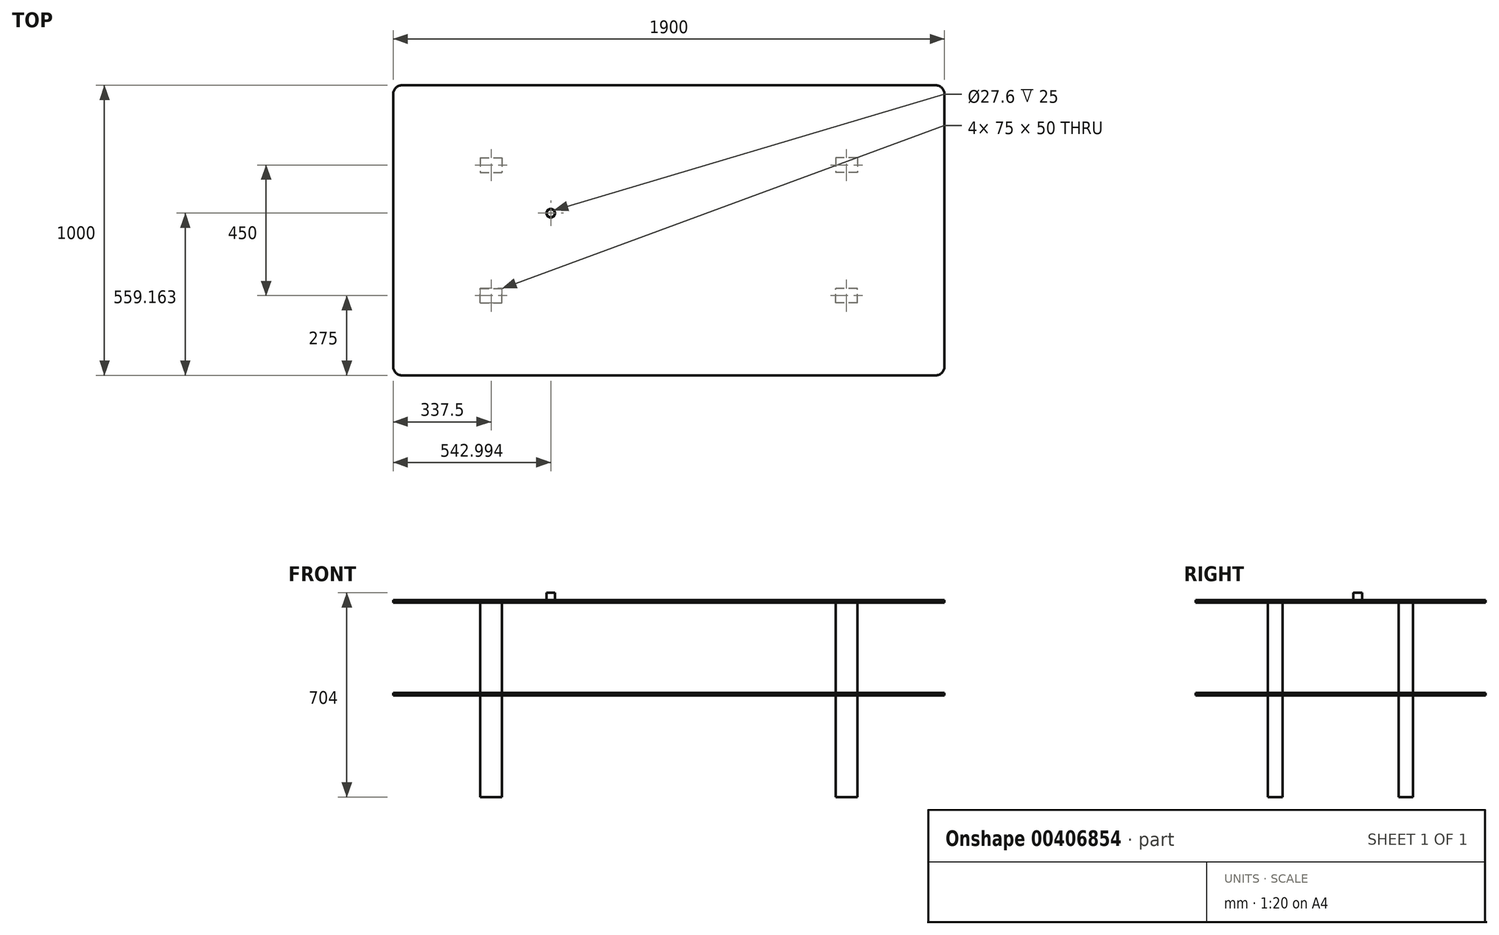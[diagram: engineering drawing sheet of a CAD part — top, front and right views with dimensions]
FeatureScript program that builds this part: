
annotation { "Feature Type Name" : "Feature", "Feature Type Description" : "" }
export const myFeature = defineFeature(function(context is Context, id is Id, definition is map)
    precondition{}
    {
        {
            var Q0;
            Q0=qCreatedBy(makeId("Top.planeOp"),FACE);
            var sketch = newSketch(context, id + "F0", { "sketchPlane" : qUnion([Q0])});
            skLineSegment(sketch, "E0.bottom", {"start": v(-920, 500) * mm, "end": v(920, 500) * mm});
            skLineSegment(sketch, "E0.top", {"start": v(-920, -500) * mm, "end": v(920, -500) * mm});
            skLineSegment(sketch, "E0.left", {"start": v(-950, 470) * mm, "end": v(-950, -470) * mm});
            skLineSegment(sketch, "E0.right", {"start": v(950, 470) * mm, "end": v(950, -470) * mm});
            skPoint(sketch, "E0.middle", {"position": v(0, 0) * mm});
            skPoint(sketch, "E1.visualSharp", {"position": v(-950, 500) * mm});
            skArc(sketch, "E1.filletArc", {"start": v(-920, 500) * mm, "mid": v(-941.21, 491.21) * mm, "end": v(-950, 470) * mm});
            skPoint(sketch, "E2.visualSharp", {"position": v(-950, -500) * mm});
            skArc(sketch, "E2.filletArc", {"start": v(-950, -470) * mm, "mid": v(-941.21, -491.21) * mm, "end": v(-920, -500) * mm});
            skPoint(sketch, "E3.visualSharp", {"position": v(950, -500) * mm});
            skArc(sketch, "E3.filletArc", {"start": v(920, -500) * mm, "mid": v(941.21, -491.21) * mm, "end": v(950, -470) * mm});
            skPoint(sketch, "E4.visualSharp", {"position": v(950, 500) * mm});
            skArc(sketch, "E4.filletArc", {"start": v(950, 470) * mm, "mid": v(941.21, 491.21) * mm, "end": v(920, 500) * mm});
            skLineSegment(sketch, "E5.bottom", {"start": v(-650, 200) * mm, "end": v(-575, 200) * mm});
            skLineSegment(sketch, "E5.top", {"start": v(-650, 250) * mm, "end": v(-575, 250) * mm});
            skLineSegment(sketch, "E5.left", {"start": v(-650, 250) * mm, "end": v(-650, 200) * mm});
            skLineSegment(sketch, "E5.right", {"start": v(-575, 250) * mm, "end": v(-575, 200) * mm});
            skLineSegment(sketch, "E6", {"start": v(0, 0) * mm, "end": v(0, 737.26) * mm, "construction": true});
            skPoint(sketch, "E6.endSnap0", {"position": v(0, 500) * mm});
            skLineSegment(sketch, "E7", {"start": v(0, 0) * mm, "end": v(1153.5, 0) * mm, "construction": true});
            skLineSegment(sketch, "E8.MirrorCS", {"start": v(575, 250) * mm, "end": v(575, 200) * mm});
            skLineSegment(sketch, "E9.MirrorCS", {"start": v(650, 250) * mm, "end": v(650, 200) * mm});
            skLineSegment(sketch, "E10.MirrorCS", {"start": v(650, 200) * mm, "end": v(575, 200) * mm});
            skLineSegment(sketch, "E11.MirrorCS", {"start": v(650, 250) * mm, "end": v(575, 250) * mm});
            skLineSegment(sketch, "E12.MirrorCS", {"start": v(-575, -250) * mm, "end": v(-575, -200) * mm});
            skLineSegment(sketch, "E13.MirrorCS", {"start": v(-650, -250) * mm, "end": v(-650, -200) * mm});
            skLineSegment(sketch, "E14.MirrorCS", {"start": v(575, -250) * mm, "end": v(575, -200) * mm});
            skLineSegment(sketch, "E15.MirrorCS", {"start": v(650, -250) * mm, "end": v(650, -200) * mm});
            skLineSegment(sketch, "E16.MirrorCS", {"start": v(650, -200) * mm, "end": v(575, -200) * mm});
            skLineSegment(sketch, "E17.MirrorCS", {"start": v(-650, -250) * mm, "end": v(-575, -250) * mm});
            skLineSegment(sketch, "E18.MirrorCS", {"start": v(-650, -200) * mm, "end": v(-575, -200) * mm});
            skLineSegment(sketch, "E19.MirrorCS", {"start": v(650, -250) * mm, "end": v(575, -250) * mm});
            skSolve(sketch);
        }
        {
            var Q0;
            Q0 = qSketchRegion(id + "F0", true);
            extrude(context, id + "F1", {"entities" : qUnion([Q0]), "depth" : 9 * mm});
        }
        {
            var Q0;
            Q0=qCreatedBy(makeId("Top.planeOp"),FACE);
            cPlane(context, id + "F2", {"entities" : qUnion([Q0]), "cplaneType" : CPlaneType.OFFSET, "offset" : 320 * mm, "width" : 150 * mm, "height" : 150 * mm});
        }
        {
            var Q0;
            Q0=qCreatedBy(id+"F2.planeOp",FACE);
            var sketch = newSketch(context, id + "F3", { "sketchPlane" : qUnion([Q0])});
            skArc(sketch, "E20.0.0", {"start": v(-950, -470) * mm, "mid": v(-941.21, -491.21) * mm, "end": v(-920, -500) * mm});
            skLineSegment(sketch, "E20.0.1", {"start": v(-920, -500) * mm, "end": v(920, -500) * mm});
            skArc(sketch, "E20.0.2", {"start": v(920, -500) * mm, "mid": v(941.21, -491.21) * mm, "end": v(950, -470) * mm});
            skLineSegment(sketch, "E20.0.3", {"start": v(950, -470) * mm, "end": v(950, 470) * mm});
            skArc(sketch, "E20.0.4", {"start": v(950, 470) * mm, "mid": v(941.21, 491.21) * mm, "end": v(920, 500) * mm});
            skLineSegment(sketch, "E20.0.5", {"start": v(920, 500) * mm, "end": v(-920, 500) * mm});
            skArc(sketch, "E20.0.6", {"start": v(-920, 500) * mm, "mid": v(-941.21, 491.21) * mm, "end": v(-950, 470) * mm});
            skLineSegment(sketch, "E20.0.7", {"start": v(-950, 470) * mm, "end": v(-950, -470) * mm});
            skSolve(sketch);
        }
        {
            var Q0;
            Q0 = qSketchRegion(id + "F3", true);
            extrude(context, id + "F4", {"entities" : qUnion([Q0]), "depth" : 9 * mm});
        }
        {
            var Q0;
            Q0=makeQuery(id+"F4.opExtrude","CAP_FACE",FACE,{"disambiguationData":[OSD([sQuery(id+"F3.wireOp",EDGE,"E20.0.0"),sQuery(id+"F3.wireOp",EDGE,"E20.0.1"),sQuery(id+"F3.wireOp",EDGE,"E20.0.2"),sQuery(id+"F3.wireOp",EDGE,"E20.0.3"),sQuery(id+"F3.wireOp",EDGE,"E20.0.4"),sQuery(id+"F3.wireOp",EDGE,"E20.0.5"),sQuery(id+"F3.wireOp",EDGE,"E20.0.6"),sQuery(id+"F3.wireOp",EDGE,"E20.0.7")])],"isStart":true});
            var sketch = newSketch(context, id + "F5", { "sketchPlane" : qUnion([Q0])});
            skLineSegment(sketch, "E21.0", {"start": v(-650, 250) * mm, "end": v(-650, 200) * mm});
            skLineSegment(sketch, "E21.1", {"start": v(-650, 250) * mm, "end": v(-575, 250) * mm});
            skLineSegment(sketch, "E21.2", {"start": v(-575, 250) * mm, "end": v(-575, 200) * mm});
            skLineSegment(sketch, "E21.3", {"start": v(-650, 200) * mm, "end": v(-575, 200) * mm});
            skLineSegment(sketch, "E22.0", {"start": v(650, 250) * mm, "end": v(575, 250) * mm});
            skLineSegment(sketch, "E22.1", {"start": v(650, 250) * mm, "end": v(650, 200) * mm});
            skLineSegment(sketch, "E22.2", {"start": v(650, 200) * mm, "end": v(575, 200) * mm});
            skLineSegment(sketch, "E22.3", {"start": v(575, 250) * mm, "end": v(575, 200) * mm});
            skLineSegment(sketch, "E22.4", {"start": v(650, -200) * mm, "end": v(575, -200) * mm});
            skLineSegment(sketch, "E22.5", {"start": v(650, -250) * mm, "end": v(650, -200) * mm});
            skLineSegment(sketch, "E22.6", {"start": v(650, -250) * mm, "end": v(575, -250) * mm});
            skLineSegment(sketch, "E22.7", {"start": v(575, -250) * mm, "end": v(575, -200) * mm});
            skLineSegment(sketch, "E22.8", {"start": v(-650, -200) * mm, "end": v(-575, -200) * mm});
            skLineSegment(sketch, "E22.9", {"start": v(-575, -250) * mm, "end": v(-575, -200) * mm});
            skLineSegment(sketch, "E22.10", {"start": v(-650, -250) * mm, "end": v(-575, -250) * mm});
            skLineSegment(sketch, "E22.11", {"start": v(-650, -250) * mm, "end": v(-650, -200) * mm});
            skSolve(sketch);
        }
        {
            var Q0;
            Q0 = qSketchRegion(id + "F5", true);
            extrude(context, id + "F6", {"entities" : qUnion([Q0]), "depth" : 670 * mm});
        }
        {
            var Q0;
            Q0=makeQuery(id+"F4.opExtrude","CAP_FACE",FACE,{"disambiguationData":[OSD([sQuery(id+"F3.wireOp",EDGE,"E20.0.0"),sQuery(id+"F3.wireOp",EDGE,"E20.0.1"),sQuery(id+"F3.wireOp",EDGE,"E20.0.2"),sQuery(id+"F3.wireOp",EDGE,"E20.0.3"),sQuery(id+"F3.wireOp",EDGE,"E20.0.4"),sQuery(id+"F3.wireOp",EDGE,"E20.0.5"),sQuery(id+"F3.wireOp",EDGE,"E20.0.6"),sQuery(id+"F3.wireOp",EDGE,"E20.0.7")])],"isStart":false});
            var sketch = newSketch(context, id + "F7", { "sketchPlane" : qUnion([Q0])});
            skCircle(sketch, "E23", {"center": v(-407, 59.16) * mm, "radius": 15 * mm});
            skCircle(sketch, "E24.0", {"center": v(-407, 59.16) * mm, "radius": 13.8 * mm});
            skLineSegment(sketch, "E25.0", {"start": v(920, 505) * mm, "end": v(-920, 505) * mm});
            skArc(sketch, "E25.1", {"start": v(955, 470) * mm, "mid": v(944.75, 494.75) * mm, "end": v(920, 505) * mm});
            skArc(sketch, "E25.2", {"start": v(-920, 505) * mm, "mid": v(-944.75, 494.75) * mm, "end": v(-955, 470) * mm});
            skLineSegment(sketch, "E25.3", {"start": v(955, -470) * mm, "end": v(955, 470) * mm});
            skLineSegment(sketch, "E25.4", {"start": v(-955, 470) * mm, "end": v(-955, -470) * mm});
            skArc(sketch, "E25.5", {"start": v(-955, -470) * mm, "mid": v(-944.75, -494.75) * mm, "end": v(-920, -505) * mm});
            skLineSegment(sketch, "E25.6", {"start": v(-920, -505) * mm, "end": v(920, -505) * mm});
            skArc(sketch, "E25.7", {"start": v(920, -505) * mm, "mid": v(944.75, -494.75) * mm, "end": v(955, -470) * mm});
            skSolve(sketch);
        }
        {
            var Q0;
            Q0=makeQuery(id+"F7.imprint","IMPRINT",FACE,{"disambiguationData":[TD([[makeQuery(id+"F7.imprint","IMPRINT",EDGE,{"derivedFrom":sQuery(id+"F7.wireOp",EDGE,"E23")}),1.0]])]});
            extrude(context, id + "F8", {"entities" : qUnion([Q0]), "depth" : 25 * mm});
        }
    });
